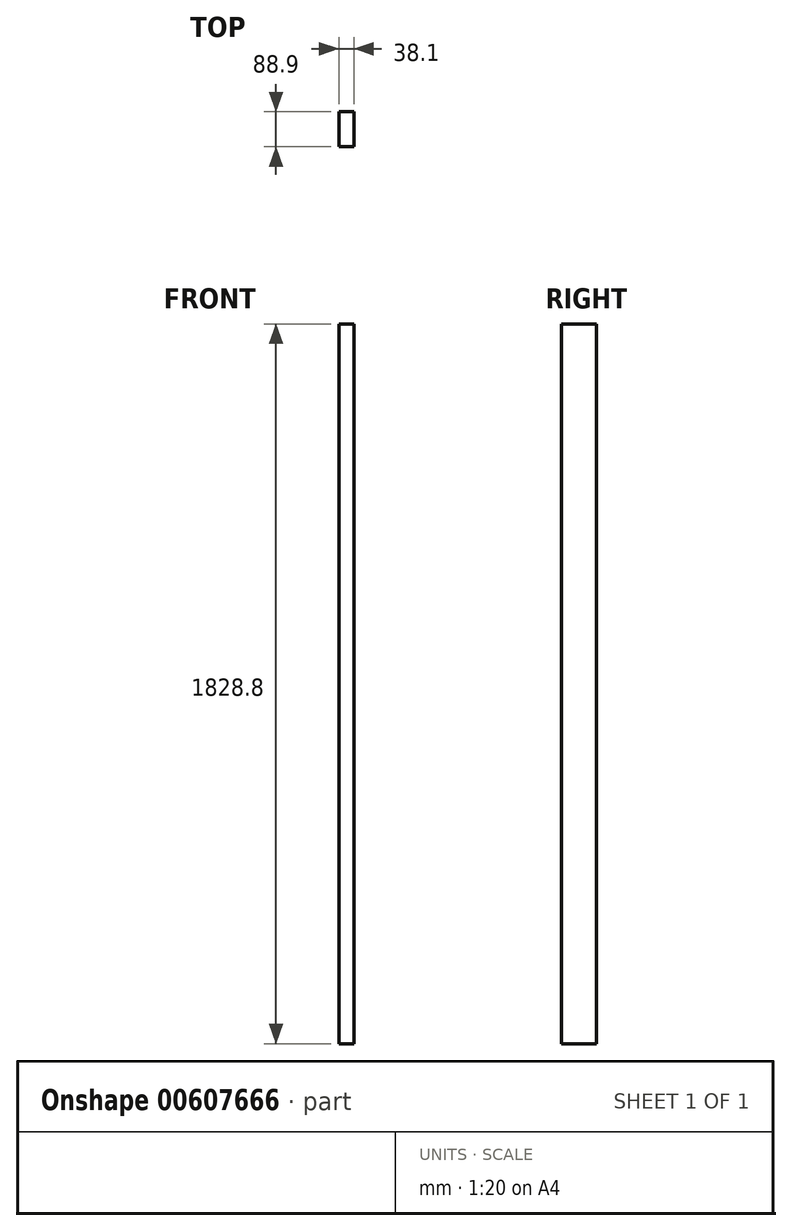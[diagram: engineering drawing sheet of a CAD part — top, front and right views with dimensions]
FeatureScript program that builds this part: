
annotation { "Feature Type Name" : "Feature", "Feature Type Description" : "" }
export const myFeature = defineFeature(function(context is Context, id is Id, definition is map)
    precondition{}
    {
        {
            var Q0;
            Q0=qCreatedBy(makeId("Front.planeOp"),FACE);
            var sketch = newSketch(context, id + "F0", { "sketchPlane" : qUnion([Q0])});
            skLineSegment(sketch, "E0", {"start": v(0, 0) * mm, "end": v(0, 1524) * mm});
            skLineSegment(sketch, "E1", {"start": v(0, 0) * mm, "end": v(0, -304.8) * mm});
            skLineSegment(sketch, "E2", {"start": v(0, -304.8) * mm, "end": v(38.1, -304.8) * mm});
            skLineSegment(sketch, "E3.bottom", {"start": v(38.1, -304.8) * mm, "end": v(0, -304.8) * mm});
            skLineSegment(sketch, "E3.top", {"start": v(38.1, 1524) * mm, "end": v(0, 1524) * mm});
            skLineSegment(sketch, "E3.left", {"start": v(38.1, -304.8) * mm, "end": v(38.1, 1524) * mm});
            skLineSegment(sketch, "E3.right", {"start": v(0, -304.8) * mm, "end": v(0, 1524) * mm});
            skSolve(sketch);
        }
        {
            var Q0;
            Q0 = qSketchRegion(id + "F0", true);
            extrude(context, id + "F1", {"entities" : qUnion([Q0]), "depth" : 88.9 * mm, "offsetDistance" : 25.4 * mm});
        }
    });
